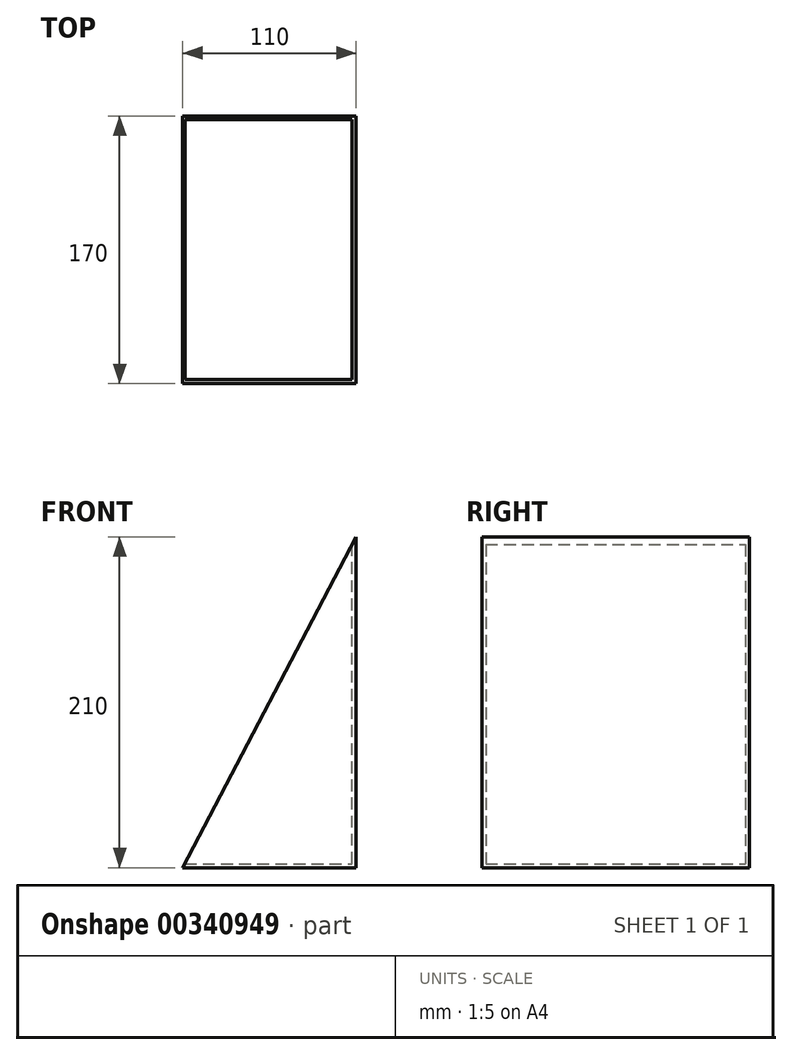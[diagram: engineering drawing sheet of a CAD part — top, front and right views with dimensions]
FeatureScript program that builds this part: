
annotation { "Feature Type Name" : "Feature", "Feature Type Description" : "" }
export const myFeature = defineFeature(function(context is Context, id is Id, definition is map)
    precondition{}
    {
        {
            var Q0;
            Q0=qCreatedBy(makeId("Front.planeOp"),FACE);
            var sketch = newSketch(context, id + "F0", { "sketchPlane" : qUnion([Q0])});
            skLineSegment(sketch, "E0", {"start": v(0, 0) * mm, "end": v(110, 0) * mm});
            skLineSegment(sketch, "E1", {"start": v(110, 0) * mm, "end": v(110, 210) * mm});
            skLineSegment(sketch, "E2", {"start": v(110, 210) * mm, "end": v(0, 0) * mm});
            skSolve(sketch);
        }
        {
            var Q0;
            Q0 = qSketchRegion(id + "F0", true);
            extrude(context, id + "F1", {"entities" : qUnion([Q0]), "depth" : 170 * mm});
        }
        {
            var Q0;
            Q0=makeQuery(id+"F1.opExtrude","SWEPT_FACE",FACE,{"disambiguationData":[OSD([sQuery(id+"F0.wireOp",EDGE,"E2")])]});
            shell(context, id + "F2", {"entities" : qUnion([Q0]), "thickness" : 2.5 * mm});
        }
    });
